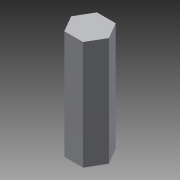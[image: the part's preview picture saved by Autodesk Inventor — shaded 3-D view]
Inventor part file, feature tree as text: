
AUTODESK INVENTOR PART (.ipt)
format: ipt  version: 2013 (Build 170138000, 138)  size: 70,144 bytes
history: native  units: in
note: dims shown in document units (in); Inventor stores cm internally (conversion verified against a paired STEP export)
features: extrude x1, sketch x1
ambient origin geometry x8: Origin, YZ Plane, XZ Plane, XY Plane, X Axis, Y Axis, Z Axis, Center Point
bodies: Solid1 (feature_tree)
feature tree (2):
  extrude  "Extrusion1"  Depth=1.25in TaperAngle=0.0deg
  sketch  "Sketch1"  dims[d0=0.375in d1=1.25in d2=0.0in]
